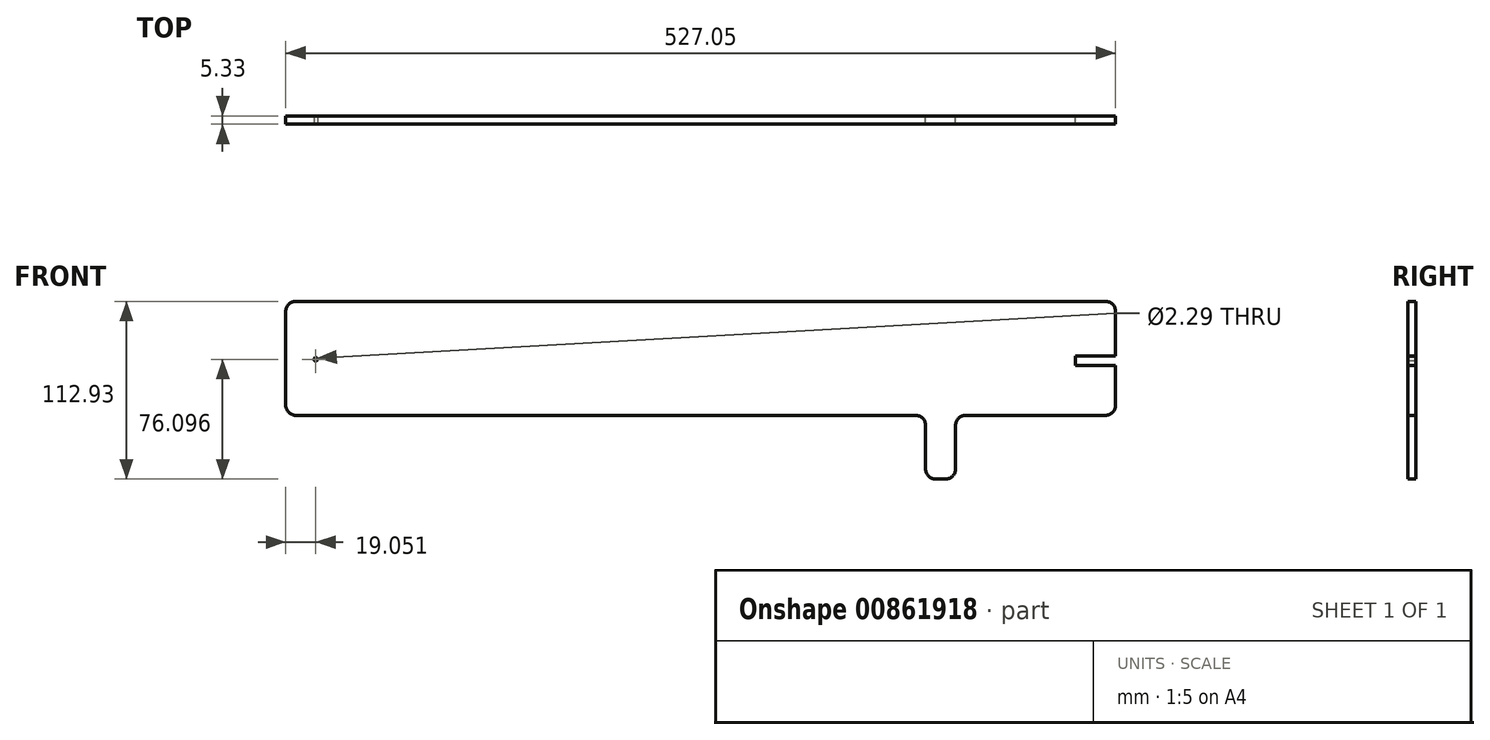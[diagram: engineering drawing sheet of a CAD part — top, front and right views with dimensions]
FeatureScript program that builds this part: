
annotation { "Feature Type Name" : "Feature", "Feature Type Description" : "" }
export const myFeature = defineFeature(function(context is Context, id is Id, definition is map)
    precondition{}
    {
        {
            var Q0;
            Q0=qCreatedBy(makeId("Front.planeOp"),FACE);
            var sketch = newSketch(context, id + "F0", { "sketchPlane" : qUnion([Q0])});
            skLineSegment(sketch, "E0.bottom", {"start": v(-81.17, 22) * mm, "end": v(433.18, 22) * mm});
            skLineSegment(sketch, "E0.top", {"start": v(-81.17, -50.4) * mm, "end": v(312.53, -50.4) * mm});
            skLineSegment(sketch, "E0.left", {"start": v(-87.52, 15.65) * mm, "end": v(-87.52, -44.04) * mm});
            skLineSegment(sketch, "E0.right", {"start": v(439.53, 15.65) * mm, "end": v(439.53, -12.8) * mm});
            skLineSegment(sketch, "E1.top", {"start": v(325.23, -90.93) * mm, "end": v(331.58, -90.93) * mm});
            skLineSegment(sketch, "E1.left", {"start": v(318.88, -56.74) * mm, "end": v(318.88, -84.58) * mm});
            skLineSegment(sketch, "E1.right", {"start": v(337.93, -56.74) * mm, "end": v(337.93, -84.58) * mm});
            skLineSegment(sketch, "E2.trimOffspring", {"start": v(344.28, -50.4) * mm, "end": v(433.18, -50.4) * mm});
            skPoint(sketch, "E3.visualSharp", {"position": v(337.93, -50.4) * mm});
            skArc(sketch, "E3.filletArc", {"start": v(344.28, -50.4) * mm, "mid": v(339.8, -52.25) * mm, "end": v(337.93, -56.74) * mm});
            skPoint(sketch, "E4.visualSharp", {"position": v(318.88, -50.4) * mm});
            skArc(sketch, "E4.filletArc", {"start": v(318.88, -56.74) * mm, "mid": v(317.02, -52.25) * mm, "end": v(312.53, -50.4) * mm});
            skPoint(sketch, "E5.visualSharp", {"position": v(439.53, -50.4) * mm});
            skArc(sketch, "E5.filletArc", {"start": v(433.18, -50.4) * mm, "mid": v(437.67, -48.53) * mm, "end": v(439.53, -44.04) * mm});
            skPoint(sketch, "E6.visualSharp", {"position": v(439.53, 22) * mm});
            skArc(sketch, "E6.filletArc", {"start": v(439.53, 15.65) * mm, "mid": v(437.67, 20.14) * mm, "end": v(433.18, 22) * mm});
            skPoint(sketch, "E7.visualSharp", {"position": v(318.88, -90.93) * mm});
            skArc(sketch, "E7.filletArc", {"start": v(318.88, -84.58) * mm, "mid": v(320.74, -89.07) * mm, "end": v(325.23, -90.93) * mm});
            skPoint(sketch, "E8.visualSharp", {"position": v(337.93, -90.93) * mm});
            skArc(sketch, "E8.filletArc", {"start": v(331.58, -90.93) * mm, "mid": v(336.07, -89.07) * mm, "end": v(337.93, -84.58) * mm});
            skPoint(sketch, "E9.visualSharp", {"position": v(-87.52, 22) * mm});
            skArc(sketch, "E9.filletArc", {"start": v(-81.17, 22) * mm, "mid": v(-85.66, 20.14) * mm, "end": v(-87.52, 15.65) * mm});
            skPoint(sketch, "E10.visualSharp", {"position": v(-87.52, -50.4) * mm});
            skArc(sketch, "E10.filletArc", {"start": v(-87.52, -44.04) * mm, "mid": v(-85.66, -48.53) * mm, "end": v(-81.17, -50.4) * mm});
            skLineSegment(sketch, "E11.bottom", {"start": v(439.53, -12.8) * mm, "end": v(414.13, -12.8) * mm});
            skLineSegment(sketch, "E11.top", {"start": v(439.53, -18.64) * mm, "end": v(414.13, -18.64) * mm});
            skLineSegment(sketch, "E11.right", {"start": v(414.13, -12.8) * mm, "end": v(414.13, -18.64) * mm});
            skLineSegment(sketch, "E12.trimOffspring", {"start": v(439.53, -18.64) * mm, "end": v(439.53, -44.04) * mm});
            skSolve(sketch);
        }
        {
            var Q0;
            Q0=makeQuery(id+"F0.imprint","IMPRINT",FACE,{"disambiguationData":[TD([[makeQuery(id+"F0.imprint","IMPRINT",EDGE,{"derivedFrom":sQuery(id+"F0.wireOp",EDGE,"E0.bottom")}),-1.0]])]});
            extrude(context, id + "F1", {"entities" : qUnion([Q0]), "depth" : 5.33 * mm, "offsetDistance" : 25.4 * mm});
        }
        {
            var Q0;
            Q0=makeQuery(id+"F1.opExtrude","CAP_FACE",FACE,{"disambiguationData":[OSD([sQuery(id+"F0.wireOp",EDGE,"E0.bottom"),sQuery(id+"F0.wireOp",EDGE,"E0.top"),sQuery(id+"F0.wireOp",EDGE,"E0.left"),sQuery(id+"F0.wireOp",EDGE,"E0.right"),sQuery(id+"F0.wireOp",EDGE,"E1.top"),sQuery(id+"F0.wireOp",EDGE,"E1.left"),sQuery(id+"F0.wireOp",EDGE,"E1.right"),sQuery(id+"F0.wireOp",EDGE,"E2.trimOffspring"),sQuery(id+"F0.wireOp",EDGE,"E3.filletArc"),sQuery(id+"F0.wireOp",EDGE,"E4.filletArc"),sQuery(id+"F0.wireOp",EDGE,"E5.filletArc"),sQuery(id+"F0.wireOp",EDGE,"E6.filletArc"),sQuery(id+"F0.wireOp",EDGE,"E7.filletArc"),sQuery(id+"F0.wireOp",EDGE,"E8.filletArc"),sQuery(id+"F0.wireOp",EDGE,"E9.filletArc"),sQuery(id+"F0.wireOp",EDGE,"E10.filletArc"),sQuery(id+"F0.wireOp",EDGE,"E11.bottom"),sQuery(id+"F0.wireOp",EDGE,"E11.top"),sQuery(id+"F0.wireOp",EDGE,"E11.right"),sQuery(id+"F0.wireOp",EDGE,"E12.trimOffspring")])],"isStart":false});
            var sketch = newSketch(context, id + "F2", { "sketchPlane" : qUnion([Q0])});
            skCircle(sketch, "E13", {"center": v(-68.47, -14.83) * mm, "radius": 1.14 * mm});
            skSolve(sketch);
        }
        {
            var Q0;
            Q0=makeQuery(id+"F2.imprint","IMPRINT",FACE,{"disambiguationData":[TD([[makeQuery(id+"F2.imprint","IMPRINT",EDGE,{"derivedFrom":sQuery(id+"F2.wireOp",EDGE,"E13")}),1.0]])]});
            extrude(context, id + "F3", {"entities" : qUnion([Q0]), "operationType" : NewBodyOperationType.REMOVE, "oppositeDirection" : true, "depth" : 25.4 * mm, "offsetDistance" : 25.4 * mm});
        }
    });
